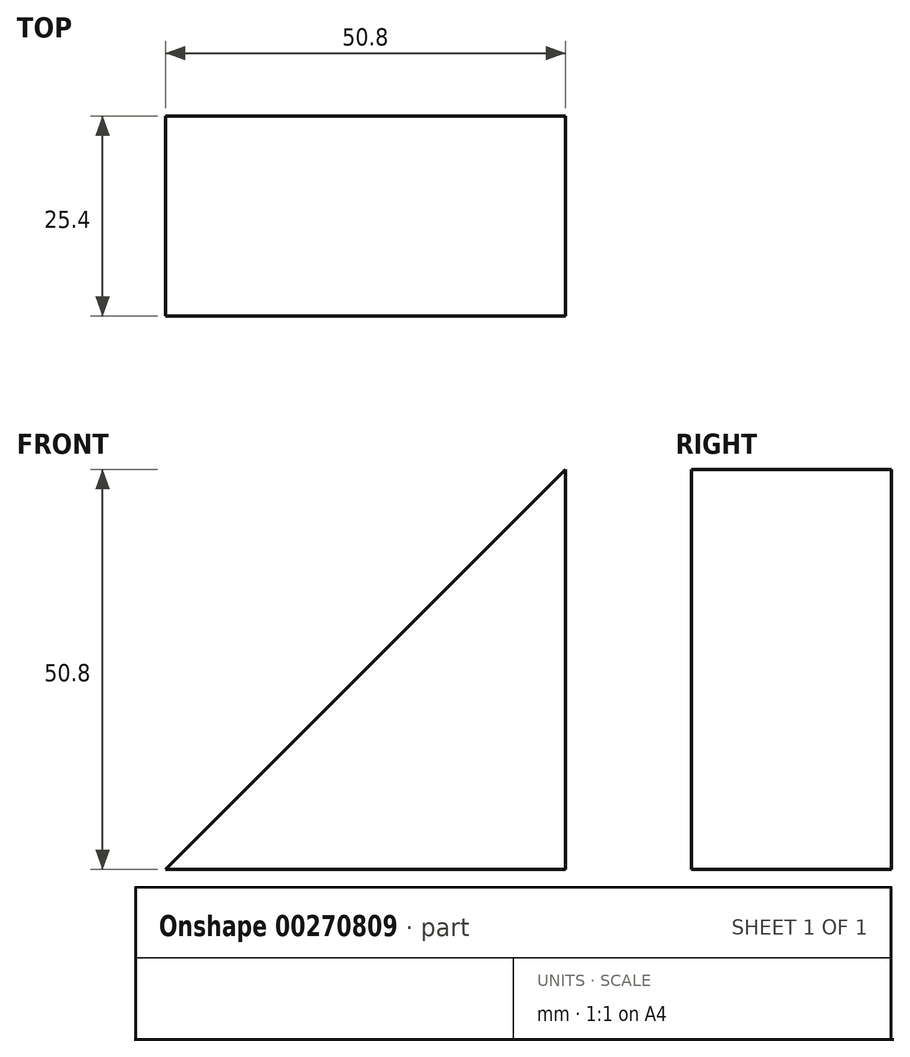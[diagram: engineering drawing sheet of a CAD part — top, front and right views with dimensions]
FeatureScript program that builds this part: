
annotation { "Feature Type Name" : "Feature", "Feature Type Description" : "" }
export const myFeature = defineFeature(function(context is Context, id is Id, definition is map)
    precondition{}
    {
        {
            var Q0;
            Q0=qCreatedBy(makeId("Front.planeOp"),FACE);
            var sketch = newSketch(context, id + "F0", { "sketchPlane" : qUnion([Q0])});
            skLineSegment(sketch, "E0", {"start": v(-50.8, 0) * mm, "end": v(0, 0) * mm});
            skLineSegment(sketch, "E1", {"start": v(0, 0) * mm, "end": v(0, 50.8) * mm});
            skLineSegment(sketch, "E2", {"start": v(0, 50.8) * mm, "end": v(-50.8, 0) * mm});
            skSolve(sketch);
        }
        {
            var Q0;
            Q0=makeQuery(id+"F0.imprint","IMPRINT",FACE,{"disambiguationData":[TD([[makeQuery(id+"F0.imprint","IMPRINT",EDGE,{"derivedFrom":sQuery(id+"F0.wireOp",EDGE,"E0")}),1.0]])]});
            extrude(context, id + "F1", {"entities" : qUnion([Q0]), "depth" : 25.4 * mm});
        }
    });
